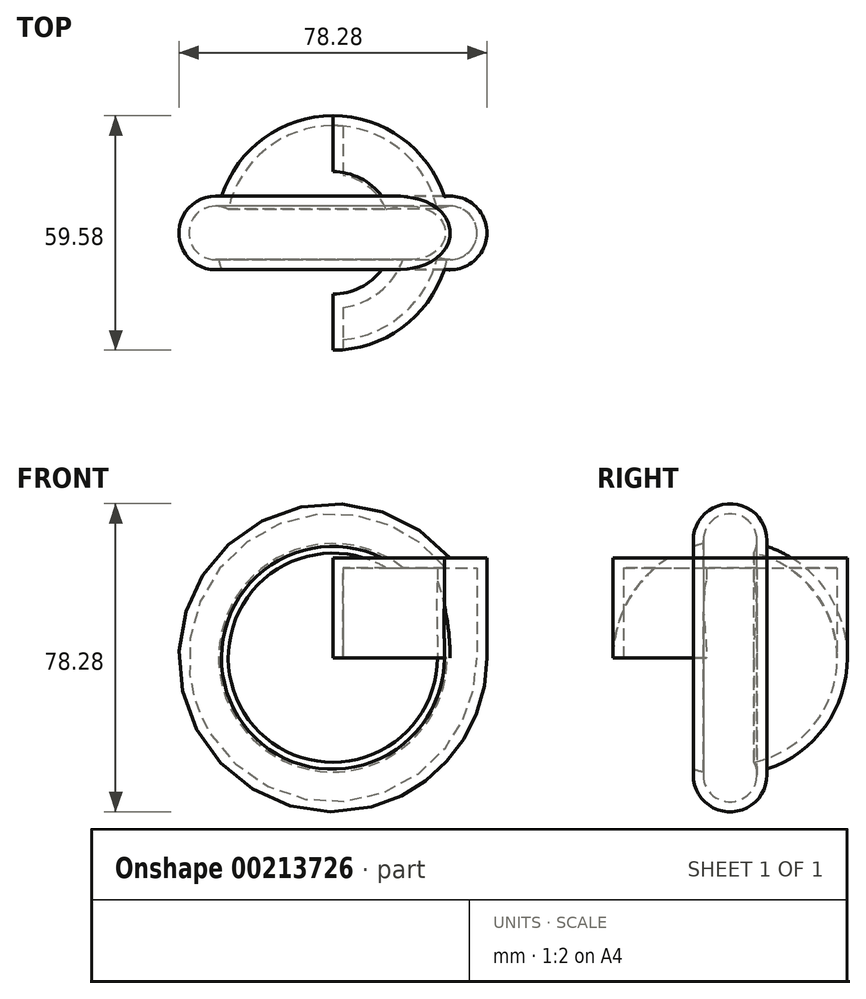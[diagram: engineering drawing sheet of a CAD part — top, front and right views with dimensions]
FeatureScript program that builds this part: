
annotation { "Feature Type Name" : "Feature", "Feature Type Description" : "" }
export const myFeature = defineFeature(function(context is Context, id is Id, definition is map)
    precondition{}
    {
        {
            var Q0;
            Q0=qCreatedBy(makeId("Top.planeOp"),FACE);
            var sketch = newSketch(context, id + "F0", { "sketchPlane" : qUnion([Q0])});
            skArc(sketch, "E0", {"start": v(0, -29.79) * mm, "mid": v(17.5, -24.1) * mm, "end": v(28.32, -9.24) * mm});
            skArc(sketch, "E1", {"start": v(28.32, -9.24) * mm, "mid": v(39.14, 0) * mm, "end": v(28.32, 9.24) * mm});
            skLineSegment(sketch, "E2", {"start": v(0, 29.79) * mm, "end": v(0, -29.79) * mm});
            skArc(sketch, "E3.trimOffspring", {"start": v(28.32, 9.24) * mm, "mid": v(17.5, 24.1) * mm, "end": v(0, 29.79) * mm});
            skSolve(sketch);
        }
        {
            var Q0;
            Q0 = qSketchRegion(id + "F0", true);
            extrude(context, id + "F1", {"entities" : qUnion([Q0]), "depth" : 25.4 * mm});
        }
        {
            var Q0;
            Q0=makeQuery(id+"F1.opExtrude","CAP_FACE",FACE,{"disambiguationData":[OSD([sQuery(id+"F0.wireOp",EDGE,"E0"),sQuery(id+"F0.wireOp",EDGE,"E1"),sQuery(id+"F0.wireOp",EDGE,"E2"),sQuery(id+"F0.wireOp",EDGE,"E3.trimOffspring")])],"isStart":true});
            var Q1;
            Q1=makeQuery(id+"F1.opExtrude","CAP_EDGE",EDGE,{"disambiguationData":[OSD([sQuery(id+"F0.wireOp",EDGE,"E2")])],"isStart":true});
            revolve(context, id + "F2", {"operationType" : NewBodyOperationType.ADD, "entities" : qUnion([Q0]), "axis" : qUnion([Q1]), "revolveType" : RevolveType.FULL});
        }
        {
            var Q0;
            Q0=makeQuery(id+"F2.opRevolve","SWEPT_FACE",FACE,{"disambiguationData":[OSD([sQuery(id+"F0.wireOp",EDGE,"E0")])]});
            shell(context, id + "F3", {"entities" : qUnion([Q0]), "thickness" : 2.54 * mm});
        }
    });
